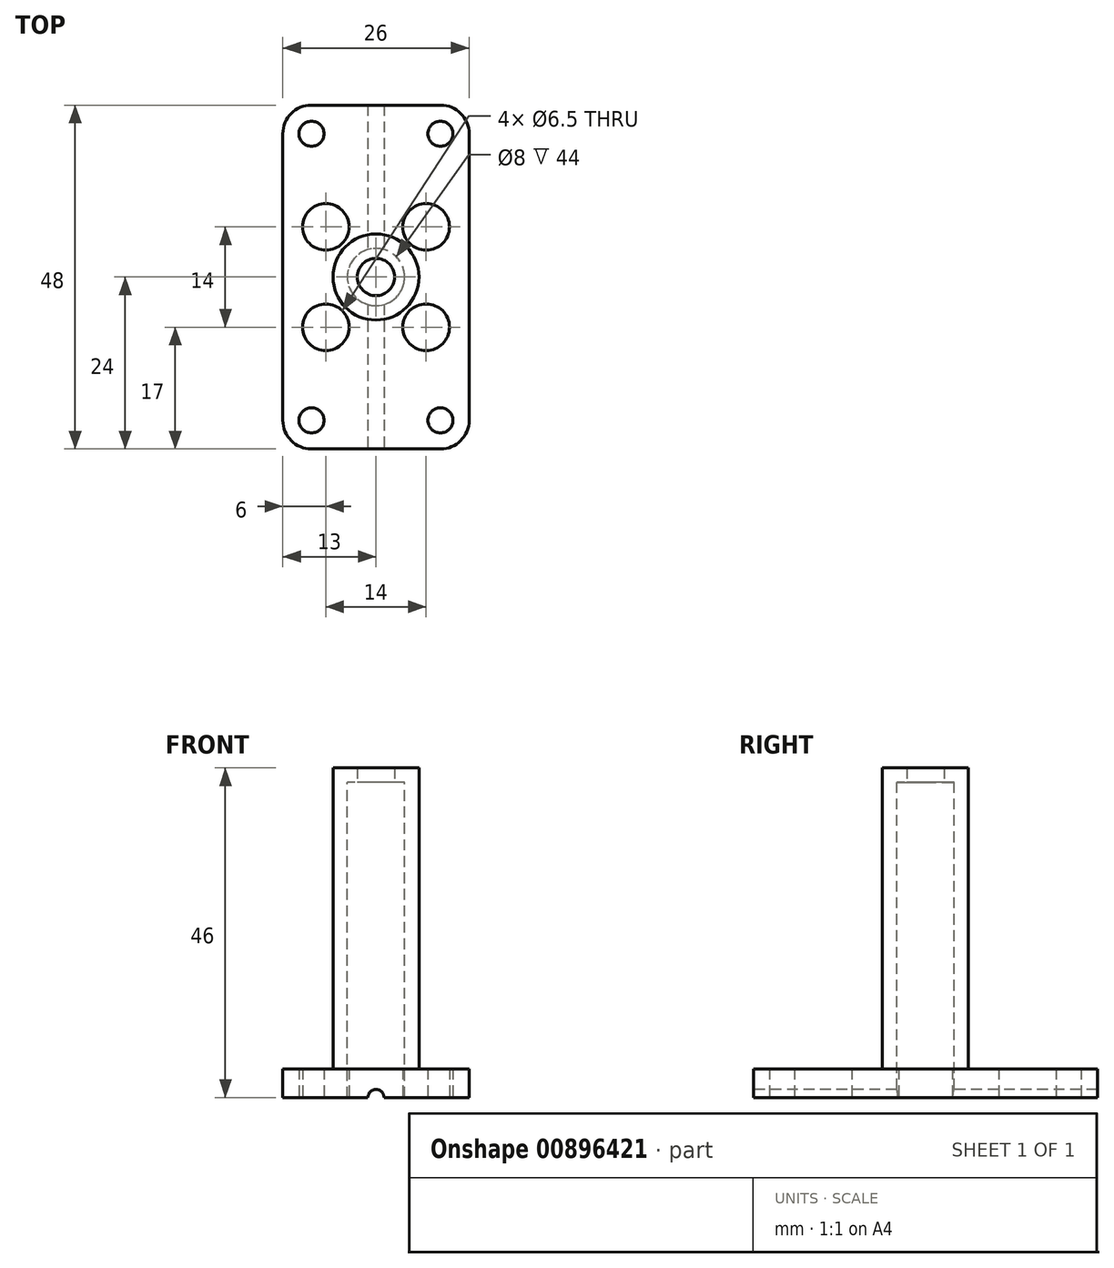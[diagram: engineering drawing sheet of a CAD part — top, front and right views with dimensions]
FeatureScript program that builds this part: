
annotation { "Feature Type Name" : "Feature", "Feature Type Description" : "" }
export const myFeature = defineFeature(function(context is Context, id is Id, definition is map)
    precondition{}
    {
        {
            var Q0;
            Q0=qCreatedBy(makeId("Top.planeOp"),FACE);
            var sketch = newSketch(context, id + "F0", { "sketchPlane" : qUnion([Q0])});
            skCircle(sketch, "E0", {"center": v(-7, 7) * mm, "radius": 3.25 * mm});
            skCircle(sketch, "E1", {"center": v(7, 7) * mm, "radius": 3.25 * mm});
            skCircle(sketch, "E2", {"center": v(7, -7) * mm, "radius": 3.25 * mm});
            skCircle(sketch, "E3", {"center": v(-7, -7) * mm, "radius": 3.25 * mm});
            skCircle(sketch, "E4", {"center": v(-9, 20) * mm, "radius": 1.75 * mm});
            skCircle(sketch, "E5", {"center": v(9, 20) * mm, "radius": 1.75 * mm});
            skCircle(sketch, "E6", {"center": v(9, -20) * mm, "radius": 1.75 * mm});
            skCircle(sketch, "E7", {"center": v(-9, -20) * mm, "radius": 1.75 * mm});
            skArc(sketch, "E8", {"start": v(-9, -24) * mm, "mid": v(-11.83, -22.83) * mm, "end": v(-13, -20) * mm});
            skArc(sketch, "E9", {"start": v(-13, 20) * mm, "mid": v(-11.83, 22.83) * mm, "end": v(-9, 24) * mm});
            skArc(sketch, "E10", {"start": v(9, 24) * mm, "mid": v(11.83, 22.83) * mm, "end": v(13, 20) * mm});
            skArc(sketch, "E11", {"start": v(13, -20) * mm, "mid": v(11.83, -22.83) * mm, "end": v(9, -24) * mm});
            skLineSegment(sketch, "E12", {"start": v(-13, -20) * mm, "end": v(-13, 20) * mm});
            skLineSegment(sketch, "E13", {"start": v(-9, 24) * mm, "end": v(9, 24) * mm});
            skLineSegment(sketch, "E14", {"start": v(13, 20) * mm, "end": v(13, -20) * mm});
            skLineSegment(sketch, "E15", {"start": v(9, -24) * mm, "end": v(-9, -24) * mm});
            skSolve(sketch);
        }
        {
            var Q0;
            Q0 = qSketchRegion(id + "F0", true);
            extrude(context, id + "F1", {"entities" : qUnion([Q0]), "depth" : 4 * mm, "offsetDistance" : 25 * mm});
        }
        {
            var Q0;
            Q0=makeQuery(id+"F1.opExtrude","SWEPT_FACE",FACE,{"disambiguationData":[OSD([sQuery(id+"F0.wireOp",EDGE,"E15")])]});
            var sketch = newSketch(context, id + "F2", { "sketchPlane" : qUnion([Q0])});
            skCircle(sketch, "E16", {"center": v(0, 0) * mm, "radius": 1.13 * mm});
            skSolve(sketch);
        }
        {
            var Q0;
            Q0 = qSketchRegion(id + "F2", true);
            extrude(context, id + "F3", {"entities" : qUnion([Q0]), "depth" : -60 * mm, "offsetDistance" : 25 * mm});
        }
        {
            var Q0;
            Q0=makeQuery(id+"F3.opExtrude","SWEPT_BODY",BODY,{"disambiguationData":[OSD([sQuery(id+"F2.wireOp",EDGE,"E16")])]});
            var Q1;
            Q1=makeQuery(id+"F1.opExtrude","SWEPT_BODY",BODY,{"disambiguationData":[OSD([sQuery(id+"F0.wireOp",EDGE,"E0"),sQuery(id+"F0.wireOp",EDGE,"E1"),sQuery(id+"F0.wireOp",EDGE,"E2"),sQuery(id+"F0.wireOp",EDGE,"E3"),sQuery(id+"F0.wireOp",EDGE,"E4"),sQuery(id+"F0.wireOp",EDGE,"E5"),sQuery(id+"F0.wireOp",EDGE,"E6"),sQuery(id+"F0.wireOp",EDGE,"E7"),sQuery(id+"F0.wireOp",EDGE,"E8"),sQuery(id+"F0.wireOp",EDGE,"E9"),sQuery(id+"F0.wireOp",EDGE,"E10"),sQuery(id+"F0.wireOp",EDGE,"E11"),sQuery(id+"F0.wireOp",EDGE,"E12"),sQuery(id+"F0.wireOp",EDGE,"E13"),sQuery(id+"F0.wireOp",EDGE,"E14"),sQuery(id+"F0.wireOp",EDGE,"E15")])]});
            booleanBodies(context, id + "F4", {"operationType" : BooleanOperationType.SUBTRACTION, "tools" : qUnion([Q0]), "targets" : qUnion([Q1])});
        }
        {
            var Q0;
            Q0=makeQuery(id+"F1.opExtrude","CAP_FACE",FACE,{"disambiguationData":[OSD([sQuery(id+"F0.wireOp",EDGE,"E0"),sQuery(id+"F0.wireOp",EDGE,"E1"),sQuery(id+"F0.wireOp",EDGE,"E2"),sQuery(id+"F0.wireOp",EDGE,"E3"),sQuery(id+"F0.wireOp",EDGE,"E4"),sQuery(id+"F0.wireOp",EDGE,"E5"),sQuery(id+"F0.wireOp",EDGE,"E6"),sQuery(id+"F0.wireOp",EDGE,"E7"),sQuery(id+"F0.wireOp",EDGE,"E8"),sQuery(id+"F0.wireOp",EDGE,"E9"),sQuery(id+"F0.wireOp",EDGE,"E10"),sQuery(id+"F0.wireOp",EDGE,"E11"),sQuery(id+"F0.wireOp",EDGE,"E12"),sQuery(id+"F0.wireOp",EDGE,"E13"),sQuery(id+"F0.wireOp",EDGE,"E14"),sQuery(id+"F0.wireOp",EDGE,"E15")])],"isStart":false});
            var sketch = newSketch(context, id + "F5", { "sketchPlane" : qUnion([Q0])});
            skCircle(sketch, "E17", {"center": v(0, 0) * mm, "radius": 6 * mm});
            skSolve(sketch);
        }
        {
            var Q0;
            Q0 = qSketchRegion(id + "F5", true);
            extrude(context, id + "F6", {"entities" : qUnion([Q0]), "operationType" : NewBodyOperationType.ADD, "depth" : 40 * mm, "offsetDistance" : 25 * mm});
        }
        {
            var Q0;
            Q0=makeQuery(id+"F6.opExtrude","CAP_FACE",FACE,{"disambiguationData":[OSD([sQuery(id+"F5.wireOp",EDGE,"E17")])],"isStart":false});
            var sketch = newSketch(context, id + "F7", { "sketchPlane" : qUnion([Q0])});
            skCircle(sketch, "E18", {"center": v(0, 0) * mm, "radius": 4 * mm});
            skSolve(sketch);
        }
        {
            var Q0;
            Q0 = qSketchRegion(id + "F7", true);
            extrude(context, id + "F8", {"entities" : qUnion([Q0]), "depth" : -50 * mm, "offsetDistance" : 25 * mm});
        }
        {
            var Q0;
            Q0=makeQuery(id+"F8.opExtrude","SWEPT_BODY",BODY,{"disambiguationData":[OSD([sQuery(id+"F7.wireOp",EDGE,"E18")])]});
            var Q1;
            Q1=makeQuery(id+"F1.opExtrude","SWEPT_BODY",BODY,{"disambiguationData":[OSD([sQuery(id+"F0.wireOp",EDGE,"E0"),sQuery(id+"F0.wireOp",EDGE,"E1"),sQuery(id+"F0.wireOp",EDGE,"E2"),sQuery(id+"F0.wireOp",EDGE,"E3"),sQuery(id+"F0.wireOp",EDGE,"E4"),sQuery(id+"F0.wireOp",EDGE,"E5"),sQuery(id+"F0.wireOp",EDGE,"E6"),sQuery(id+"F0.wireOp",EDGE,"E7"),sQuery(id+"F0.wireOp",EDGE,"E8"),sQuery(id+"F0.wireOp",EDGE,"E9"),sQuery(id+"F0.wireOp",EDGE,"E10"),sQuery(id+"F0.wireOp",EDGE,"E11"),sQuery(id+"F0.wireOp",EDGE,"E12"),sQuery(id+"F0.wireOp",EDGE,"E13"),sQuery(id+"F0.wireOp",EDGE,"E14"),sQuery(id+"F0.wireOp",EDGE,"E15")])]});
            booleanBodies(context, id + "F9", {"operationType" : BooleanOperationType.SUBTRACTION, "tools" : qUnion([Q0]), "targets" : qUnion([Q1])});
        }
        {
            var Q0;
            Q0=makeQuery(id+"F6.opExtrude","CAP_FACE",FACE,{"disambiguationData":[OSD([sQuery(id+"F5.wireOp",EDGE,"E17")])],"isStart":false});
            var sketch = newSketch(context, id + "F10", { "sketchPlane" : qUnion([Q0])});
            skCircle(sketch, "E19", {"center": v(0, 0) * mm, "radius": 6 * mm});
            skCircle(sketch, "E20", {"center": v(0, 0) * mm, "radius": 2.6 * mm});
            skSolve(sketch);
        }
        {
            var Q0;
            Q0 = qSketchRegion(id + "F10", true);
            extrude(context, id + "F11", {"entities" : qUnion([Q0]), "operationType" : NewBodyOperationType.ADD, "depth" : 2 * mm, "offsetDistance" : 25 * mm});
        }
    });
